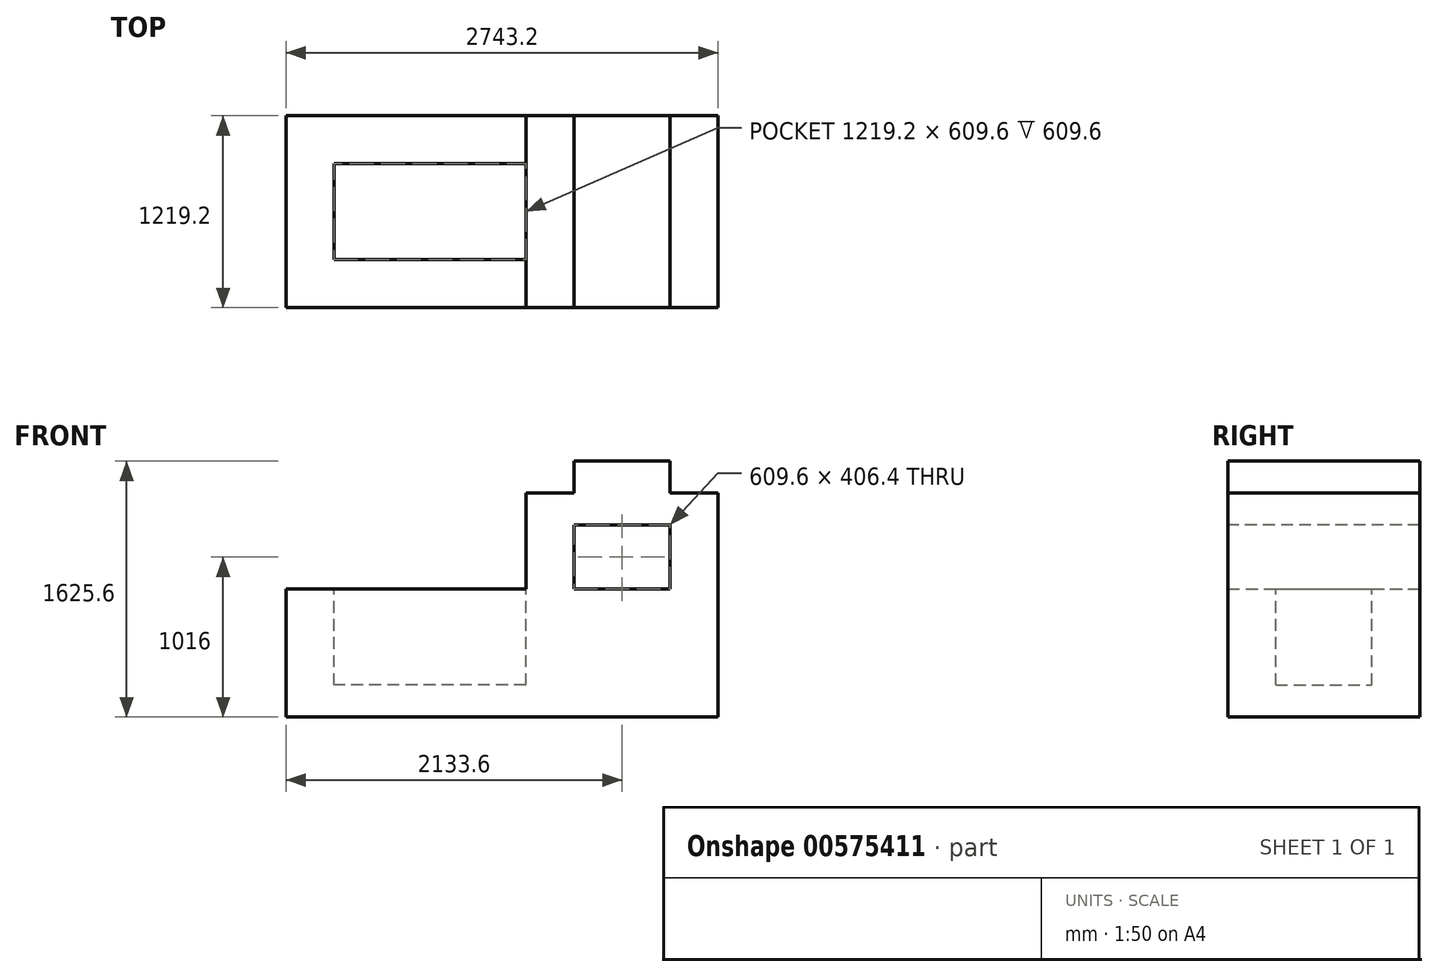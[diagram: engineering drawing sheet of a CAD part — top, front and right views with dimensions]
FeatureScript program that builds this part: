
annotation { "Feature Type Name" : "Feature", "Feature Type Description" : "" }
export const myFeature = defineFeature(function(context is Context, id is Id, definition is map)
    precondition{}
    {
        {
            var Q0;
            Q0=qCreatedBy(makeId("Front.planeOp"),FACE);
            var sketch = newSketch(context, id + "F0", { "sketchPlane" : qUnion([Q0])});
            skLineSegment(sketch, "E0", {"start": v(-1114.7, -56.32) * mm, "end": v(1628.5, -56.32) * mm});
            skLineSegment(sketch, "E1", {"start": v(1628.5, -56.32) * mm, "end": v(1628.5, 1366.08) * mm});
            skLineSegment(sketch, "E2", {"start": v(1628.5, 1366.08) * mm, "end": v(1323.7, 1366.08) * mm});
            skLineSegment(sketch, "E3", {"start": v(1323.7, 1366.08) * mm, "end": v(1323.7, 1569.28) * mm});
            skLineSegment(sketch, "E4", {"start": v(1323.7, 1569.28) * mm, "end": v(714.1, 1569.28) * mm});
            skLineSegment(sketch, "E5", {"start": v(714.1, 1569.28) * mm, "end": v(714.1, 1366.08) * mm});
            skLineSegment(sketch, "E6", {"start": v(714.1, 1366.08) * mm, "end": v(409.3, 1366.08) * mm});
            skLineSegment(sketch, "E7", {"start": v(409.3, 1366.08) * mm, "end": v(409.3, 756.48) * mm});
            skLineSegment(sketch, "E8", {"start": v(409.3, 756.48) * mm, "end": v(-1114.7, 756.48) * mm});
            skLineSegment(sketch, "E9", {"start": v(-1114.7, 756.48) * mm, "end": v(-1114.7, -56.32) * mm});
            skSolve(sketch);
        }
        {
            var Q0;
            Q0=makeQuery(id+"F0.imprint","IMPRINT",FACE,{"disambiguationData":[TD([[makeQuery(id+"F0.imprint","IMPRINT",EDGE,{"derivedFrom":sQuery(id+"F0.wireOp",EDGE,"E0")}),1.0]])]});
            extrude(context, id + "F1", {"entities" : qUnion([Q0]), "depth" : 1219.2 * mm, "offsetDistance" : 25.4 * mm});
        }
        {
            var Q0;
            Q0=makeQuery(id+"F1.opExtrude","CAP_FACE",FACE,{"disambiguationData":[OSD([sQuery(id+"F0.wireOp",EDGE,"E0"),sQuery(id+"F0.wireOp",EDGE,"E1"),sQuery(id+"F0.wireOp",EDGE,"E2"),sQuery(id+"F0.wireOp",EDGE,"E3"),sQuery(id+"F0.wireOp",EDGE,"E4"),sQuery(id+"F0.wireOp",EDGE,"E5"),sQuery(id+"F0.wireOp",EDGE,"E6"),sQuery(id+"F0.wireOp",EDGE,"E7"),sQuery(id+"F0.wireOp",EDGE,"E8"),sQuery(id+"F0.wireOp",EDGE,"E9")])],"isStart":false});
            var sketch = newSketch(context, id + "F2", { "sketchPlane" : qUnion([Q0])});
            skLineSegment(sketch, "E10", {"start": v(714.1, 1162.88) * mm, "end": v(714.1, 756.48) * mm});
            skLineSegment(sketch, "E11", {"start": v(714.1, 756.48) * mm, "end": v(1323.7, 756.48) * mm});
            skLineSegment(sketch, "E12", {"start": v(1323.7, 756.48) * mm, "end": v(1323.7, 1162.88) * mm});
            skLineSegment(sketch, "E13", {"start": v(1323.7, 1162.88) * mm, "end": v(714.1, 1162.88) * mm});
            skSolve(sketch);
        }
        {
            var Q0;
            Q0=makeQuery(id+"F2.imprint","IMPRINT",FACE,{"disambiguationData":[TD([[makeQuery(id+"F2.imprint","IMPRINT",EDGE,{"derivedFrom":sQuery(id+"F2.wireOp",EDGE,"E10")}),1.0]])]});
            extrude(context, id + "F3", {"entities" : qUnion([Q0]), "operationType" : NewBodyOperationType.REMOVE, "endBound" : BoundingType.THROUGH_ALL, "oppositeDirection" : true, "depth" : 25.4 * mm, "offsetDistance" : 25.4 * mm});
        }
        {
            var Q0;
            Q0=makeQuery(id+"F1.opExtrude","SWEPT_FACE",FACE,{"disambiguationData":[OSD([sQuery(id+"F0.wireOp",EDGE,"E8")])]});
            var sketch = newSketch(context, id + "F4", { "sketchPlane" : qUnion([Q0])});
            skLineSegment(sketch, "E14", {"start": v(409.3, -1219.2) * mm, "end": v(409.3, -914.4) * mm});
            skLineSegment(sketch, "E15", {"start": v(409.3, -914.4) * mm, "end": v(-809.9, -914.4) * mm});
            skLineSegment(sketch, "E16", {"start": v(-809.9, -914.4) * mm, "end": v(-809.9, -304.8) * mm});
            skLineSegment(sketch, "E17", {"start": v(-809.9, -304.8) * mm, "end": v(409.3, -304.8) * mm});
            skLineSegment(sketch, "E18", {"start": v(409.3, -304.8) * mm, "end": v(409.3, -914.4) * mm});
            skSolve(sketch);
        }
        {
            var Q0;
            Q0 = qSketchRegion(id + "F4", true);
            extrude(context, id + "F5", {"entities" : qUnion([Q0]), "operationType" : NewBodyOperationType.REMOVE, "oppositeDirection" : true, "depth" : 609.6 * mm, "offsetDistance" : 25.4 * mm});
        }
    });
